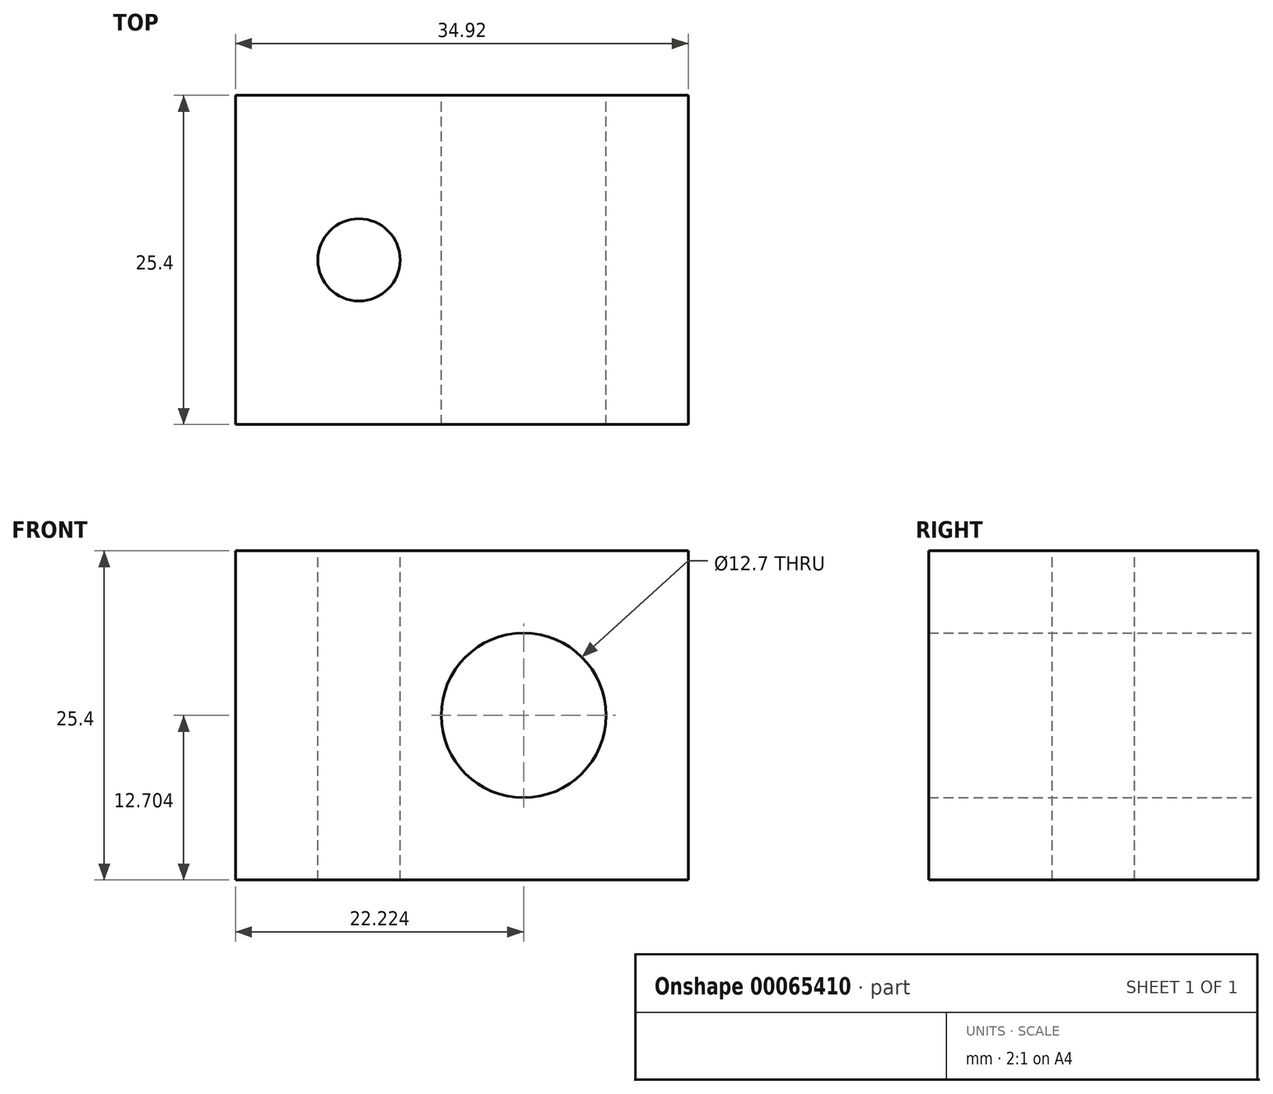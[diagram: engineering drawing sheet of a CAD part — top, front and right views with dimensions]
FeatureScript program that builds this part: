
annotation { "Feature Type Name" : "Feature", "Feature Type Description" : "" }
export const myFeature = defineFeature(function(context is Context, id is Id, definition is map)
    precondition{}
    {
        {
            var Q0;
            Q0=qCreatedBy(makeId("Front.planeOp"),FACE);
            var sketch = newSketch(context, id + "F0", { "sketchPlane" : qUnion([Q0])});
            skLineSegment(sketch, "E0.bottom", {"start": v(-6.46, 9.5) * mm, "end": v(28.46, 9.5) * mm});
            skLineSegment(sketch, "E0.top", {"start": v(-6.46, -15.9) * mm, "end": v(28.46, -15.9) * mm});
            skLineSegment(sketch, "E0.left", {"start": v(-6.46, 9.5) * mm, "end": v(-6.46, -15.9) * mm});
            skLineSegment(sketch, "E0.right", {"start": v(28.46, 9.5) * mm, "end": v(28.46, -15.9) * mm});
            skLineSegment(sketch, "E1", {"start": v(28.46, -3.2) * mm, "end": v(15.76, -3.2) * mm});
            skCircle(sketch, "E2", {"center": v(15.76, -3.2) * mm, "radius": 6.35 * mm});
            skSolve(sketch);
        }
        {
            var Q0;
            {var subQ1=sQuery(id+"F0.wireOp",EDGE,"E0.bottom");Q0=makeQuery(id+"F0.imprint","IMPRINT",FACE,{"disambiguationData":[TD([[makeQuery(id+"F0.imprint","IMPRINT",EDGE,{"derivedFrom":subQ1}),-1.0]])]});}
            extrude(context, id + "F1", {"entities" : qUnion([Q0]), "depth" : 25.4 * mm});
        }
        {
            var Q0;
            Q0=makeQuery(id+"F1.opExtrude","SWEPT_FACE",FACE,{"disambiguationData":[OSD([sQuery(id+"F0.wireOp",EDGE,"E0.bottom")])]});
            var sketch = newSketch(context, id + "F2", { "sketchPlane" : qUnion([Q0])});
            skLineSegment(sketch, "E3", {"start": v(28.46, -12.7) * mm, "end": v(3.06, -12.7) * mm});
            skPoint(sketch, "E3.endSnap0", {"position": v(28.46, -12.7) * mm});
            skCircle(sketch, "E4", {"center": v(3.06, -12.7) * mm, "radius": 3.18 * mm});
            skSolve(sketch);
        }
        {
            var Q0;
            Q0=makeQuery(id+"F2.imprint","IMPRINT",FACE,{"disambiguationData":[TD([[makeQuery(id+"F2.imprint","IMPRINT",EDGE,{"derivedFrom":sQuery(id+"F2.wireOp",EDGE,"E4")}),1.0]])]});
            extrude(context, id + "F3", {"entities" : qUnion([Q0]), "operationType" : NewBodyOperationType.REMOVE, "oppositeDirection" : true, "depth" : 50.8 * mm});
        }
    });
